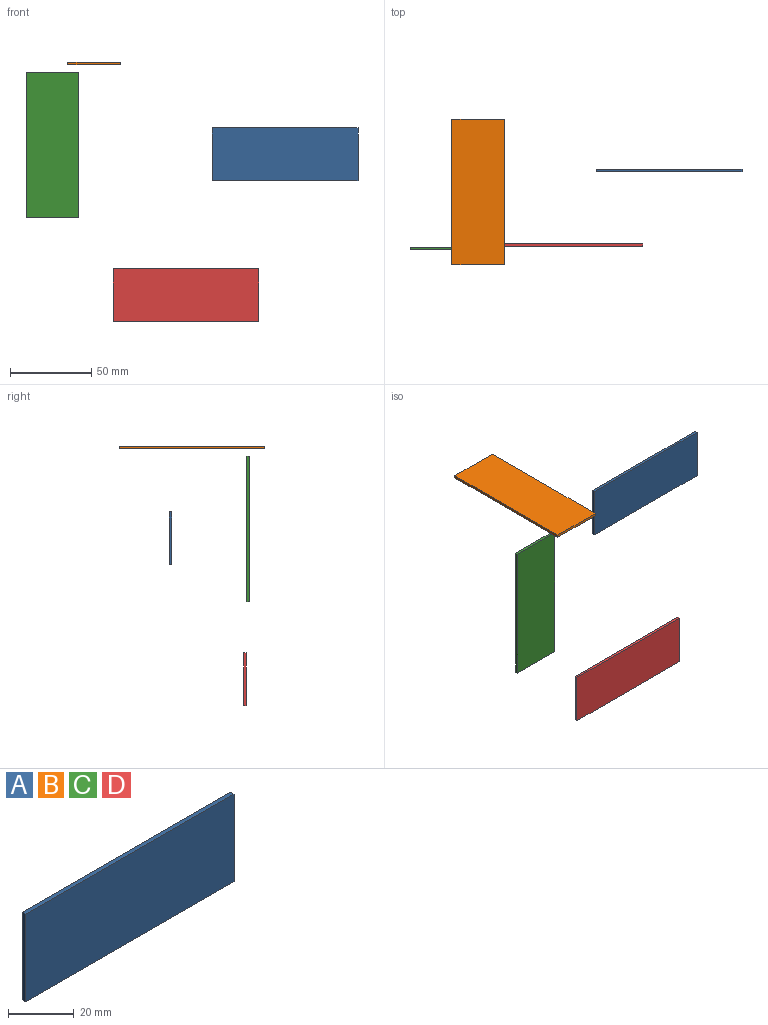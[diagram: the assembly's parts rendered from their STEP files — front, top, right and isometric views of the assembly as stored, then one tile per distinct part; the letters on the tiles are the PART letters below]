
ASSEMBLY  parts=4 mates=2
PART A: 6 faces, bbox 89.5x1.6x32.6 mm
  f0: plane 89.51x1.64mm, normal (0,0,1), area 146.5mm2, adj f1,f3,f4,f5
  f1: plane 32.58x1.64mm, normal (-1,0,0), area 53.3mm2, adj f0,f2,f4,f5
  f2: plane 89.51x1.64mm, normal (0,0,-1), area 146.5mm2, adj f1,f3,f4,f5
  f3: plane 32.58x1.64mm, normal (1,0,0), area 53.3mm2, adj f0,f2,f4,f5
  f4: plane 89.51x32.58mm, normal (0,-1,0), area 2916mm2, adj f0,f1,f2,f3
  f5: plane 89.51x32.58mm, normal (0,1,0), area 2916mm2, adj f0,f1,f2,f3
PART B: same geometry as A
PART C: same geometry as A
PART D: same geometry as A
PLACE A t=(72.77,6.83,-65.3)mm
PLACE B rot(axis=(-0.58,0.58,-0.58),120deg) t=(-44.6,-7.28,-10.3)mm
PLACE C rot(axis=(0,-1,0),90deg) t=(-70.33,-41.1,-59.6)mm
PLACE D t=(11.89,-38.99,-151.9)mm
MATE parallel C.f3 <-> B.f4  axis (0,0,1) through (-54.04,-42.74,-14.85)mm
MATE parallel C.f4 <-> C.f4  axis (0,-1,0) through (-70.33,-42.74,-59.6)mm
